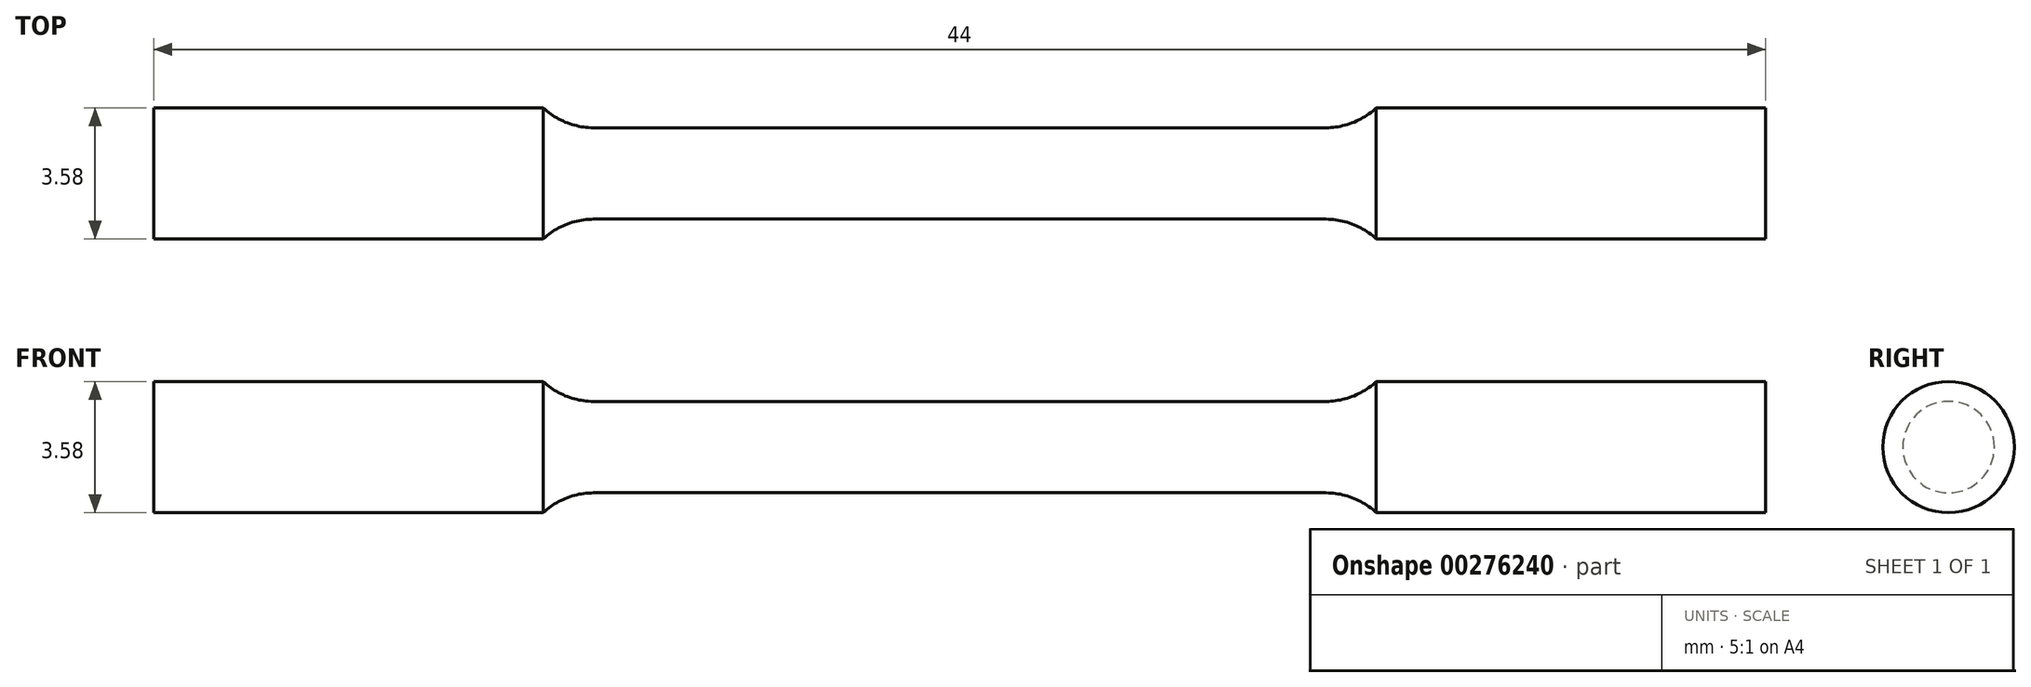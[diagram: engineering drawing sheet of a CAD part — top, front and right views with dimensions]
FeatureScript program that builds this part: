
annotation { "Feature Type Name" : "Feature", "Feature Type Description" : "" }
export const myFeature = defineFeature(function(context is Context, id is Id, definition is map)
    precondition{}
    {
        {
            var Q0;
            Q0=qCreatedBy(makeId("Front.planeOp"),FACE);
            var sketch = newSketch(context, id + "F0", { "sketchPlane" : qUnion([Q0])});
            skLineSegment(sketch, "E0", {"start": v(0, 1.25) * mm, "end": v(10, 1.25) * mm});
            skArc(sketch, "E1", {"start": v(10, 1.25) * mm, "mid": v(10.74, 1.4) * mm, "end": v(11.37, 1.8) * mm});
            skLineSegment(sketch, "E2", {"start": v(11.37, 1.8) * mm, "end": v(22, 1.8) * mm});
            skLineSegment(sketch, "E3", {"start": v(22, 1.8) * mm, "end": v(22, 0) * mm});
            skLineSegment(sketch, "E4", {"start": v(22, 0) * mm, "end": v(0, 0) * mm});
            skLineSegment(sketch, "E5.MirrorCS", {"start": v(0, 1.25) * mm, "end": v(-10, 1.25) * mm});
            skLineSegment(sketch, "E6.MirrorCS", {"start": v(-22, 0) * mm, "end": v(0, 0) * mm});
            skLineSegment(sketch, "E7.MirrorCS", {"start": v(-11.37, 1.8) * mm, "end": v(-22, 1.8) * mm});
            skLineSegment(sketch, "E8.MirrorCS", {"start": v(-22, 1.8) * mm, "end": v(-22, 0) * mm});
            skArc(sketch, "E9.MirrorCS", {"start": v(-10, 1.25) * mm, "mid": v(-10.74, 1.4) * mm, "end": v(-11.37, 1.8) * mm});
            skSolve(sketch);
        }
        {
            var Q0;
            Q0 = qSketchRegion(id + "F0", true);
            var Q1;
            Q1=sQuery(id+"F0.wireOp",EDGE,"E6.MirrorCS");
            revolve(context, id + "F1", {"entities" : qUnion([Q0]), "axis" : qUnion([Q1]), "revolveType" : RevolveType.FULL});
        }
    });
